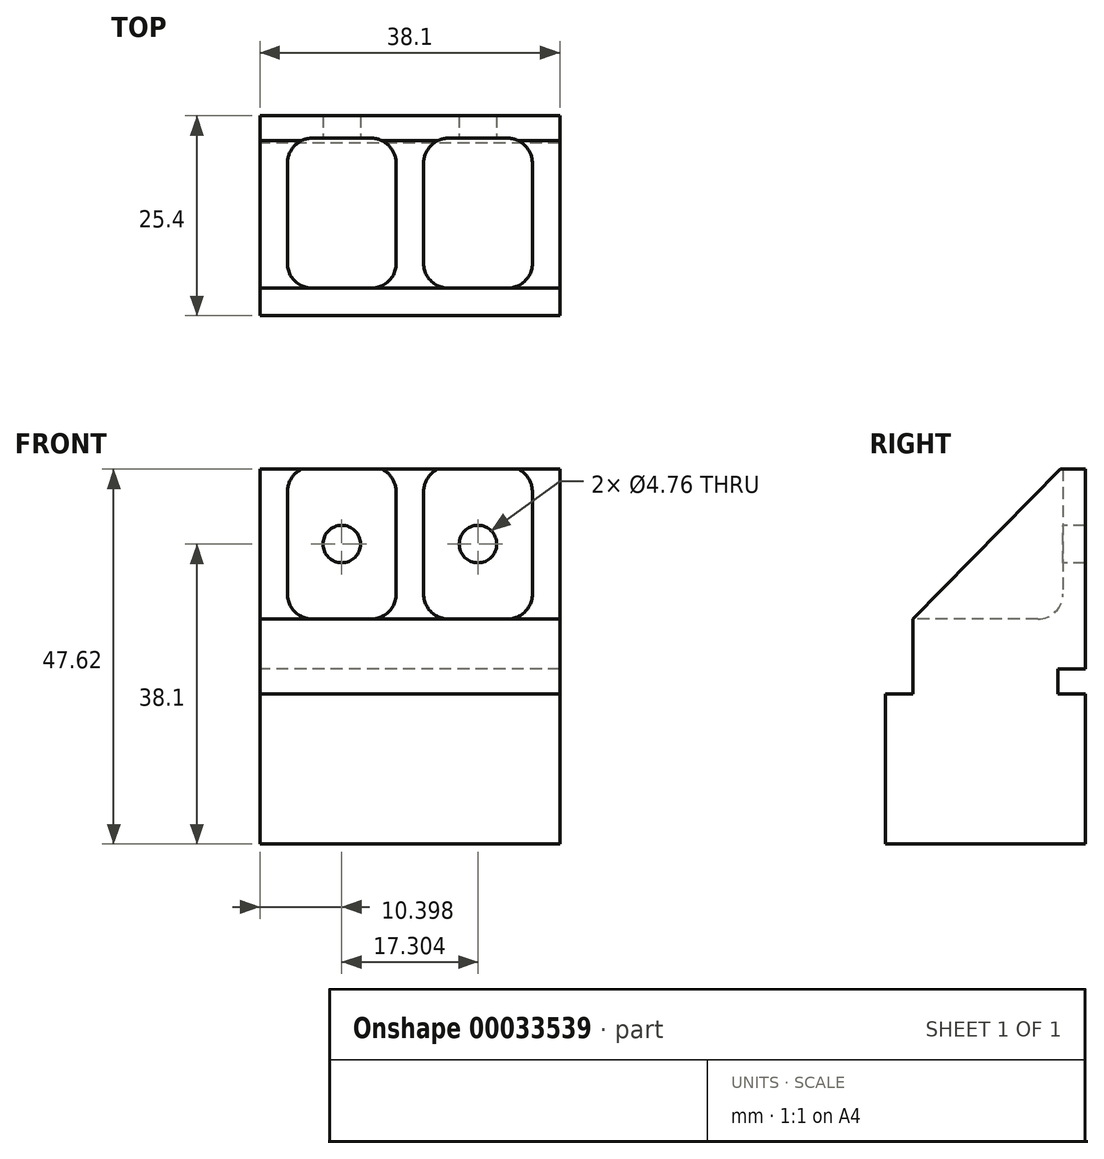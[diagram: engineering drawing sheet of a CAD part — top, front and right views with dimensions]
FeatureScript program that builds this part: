
annotation { "Feature Type Name" : "Feature", "Feature Type Description" : "" }
export const myFeature = defineFeature(function(context is Context, id is Id, definition is map)
    precondition{}
    {
        {
            var Q0;
            Q0=qCreatedBy(makeId("Right.planeOp"),FACE);
            var sketch = newSketch(context, id + "F0", { "sketchPlane" : qUnion([Q0])});
            skLineSegment(sketch, "E0.bottom", {"start": v(0, 0) * mm, "end": v(25.4, 0) * mm});
            skLineSegment(sketch, "E0.top", {"start": v(0, 19.05) * mm, "end": v(3.5, 19.05) * mm});
            skLineSegment(sketch, "E0.left", {"start": v(0, 0) * mm, "end": v(0, 19.05) * mm});
            skLineSegment(sketch, "E0.right", {"start": v(25.4, 0) * mm, "end": v(25.4, 19.05) * mm});
            skLineSegment(sketch, "E1", {"start": v(21.9, 19.05) * mm, "end": v(21.9, 22.23) * mm});
            skLineSegment(sketch, "E2", {"start": v(21.9, 22.23) * mm, "end": v(25.4, 22.23) * mm});
            skLineSegment(sketch, "E3", {"start": v(25.4, 22.23) * mm, "end": v(25.4, 47.62) * mm});
            skLineSegment(sketch, "E4", {"start": v(25.4, 47.62) * mm, "end": v(22.23, 47.62) * mm});
            skLineSegment(sketch, "E5", {"start": v(22.23, 47.62) * mm, "end": v(22.23, 28.58) * mm});
            skLineSegment(sketch, "E6", {"start": v(22.23, 28.58) * mm, "end": v(3.5, 28.57) * mm});
            skLineSegment(sketch, "E7", {"start": v(3.5, 28.57) * mm, "end": v(3.5, 19.05) * mm});
            skLineSegment(sketch, "E8.trimOffspring", {"start": v(21.9, 19.05) * mm, "end": v(25.4, 19.05) * mm});
            skLineSegment(sketch, "E9", {"start": v(3.5, 28.57) * mm, "end": v(22.23, 47.62) * mm});
            skSolve(sketch);
        }
        {
            var Q0;
            Q0=makeQuery(id+"F0.imprint","IMPRINT",FACE,{"disambiguationData":[TD([[makeQuery(id+"F0.imprint","IMPRINT",EDGE,{"derivedFrom":sQuery(id+"F0.wireOp",EDGE,"E0.bottom")}),1.0]])]});
            var Q1;
            Q1=makeQuery(id+"F0.imprint","IMPRINT",FACE,{"disambiguationData":[TD([[makeQuery(id+"F0.imprint","IMPRINT",EDGE,{"derivedFrom":sQuery(id+"F0.wireOp",EDGE,"E5")}),-1.0]])]});
            extrude(context, id + "F1", {"entities" : qUnion([Q0, Q1]), "depth" : 38.1 * mm});
        }
        {
            var Q0;
            Q0=makeQuery(id+"F1.opExtrude","SWEPT_FACE",FACE,{"disambiguationData":[OSD([sQuery(id+"F0.wireOp",EDGE,"E7")])]});
            var sketch = newSketch(context, id + "F2", { "sketchPlane" : qUnion([Q0])});
            skLineSegment(sketch, "E10.bottom", {"start": v(3.5, 47.62) * mm, "end": v(17.3, 47.62) * mm});
            skLineSegment(sketch, "E10.top", {"start": v(3.5, 28.57) * mm, "end": v(17.3, 28.57) * mm});
            skLineSegment(sketch, "E10.left", {"start": v(3.5, 47.62) * mm, "end": v(3.5, 28.57) * mm});
            skLineSegment(sketch, "E10.right", {"start": v(17.3, 47.62) * mm, "end": v(17.3, 28.57) * mm});
            skLineSegment(sketch, "E11.bottom", {"start": v(20.8, 47.62) * mm, "end": v(34.6, 47.62) * mm});
            skLineSegment(sketch, "E11.top", {"start": v(20.8, 28.57) * mm, "end": v(34.6, 28.57) * mm});
            skLineSegment(sketch, "E11.left", {"start": v(20.8, 47.62) * mm, "end": v(20.8, 28.57) * mm});
            skLineSegment(sketch, "E11.right", {"start": v(34.6, 47.62) * mm, "end": v(34.6, 28.57) * mm});
            skSolve(sketch);
        }
        {
            var Q0;
            Q0=makeQuery(id+"F2.imprint","IMPRINT",FACE,{"disambiguationData":[TD([[makeQuery(id+"F2.imprint","IMPRINT",EDGE,{"derivedFrom":sQuery(id+"F2.wireOp",EDGE,"E11.bottom")}),-1.0]])]});
            var Q1;
            Q1=makeQuery(id+"F2.imprint","IMPRINT",FACE,{"disambiguationData":[TD([[makeQuery(id+"F2.imprint","IMPRINT",EDGE,{"derivedFrom":sQuery(id+"F2.wireOp",EDGE,"E10.bottom")}),-1.0]])]});
            extrude(context, id + "F3", {"entities" : qUnion([Q0, Q1]), "operationType" : NewBodyOperationType.REMOVE, "oppositeDirection" : true, "depth" : 19.05 * mm});
        }
        {
            var Q0;
            Q0=makeQuery(id+"F3.boolean.opBoolean","COPY",EDGE,{"derivedFrom":makeQuery(id+"F3.opExtrude","CAP_EDGE",EDGE,{"disambiguationData":[OSD([sQuery(id+"F2.wireOp",EDGE,"E10.top")])],"isStart":false})});
            var Q1;
            Q1=makeQuery(id+"F3.boolean.opBoolean","COPY",EDGE,{"derivedFrom":makeQuery(id+"F3.opExtrude","CAP_EDGE",EDGE,{"disambiguationData":[OSD([sQuery(id+"F2.wireOp",EDGE,"E11.top")])],"isStart":false})});
            var Q2;
            Q2=makeQuery(id+"F3.boolean.opBoolean","COPY",EDGE,{"derivedFrom":makeQuery(id+"F3.opExtrude","CAP_EDGE",EDGE,{"disambiguationData":[OSD([sQuery(id+"F2.wireOp",EDGE,"E11.left")])],"isStart":false})});
            var Q3;
            Q3=makeQuery(id+"F3.boolean.opBoolean","COPY",EDGE,{"derivedFrom":makeQuery(id+"F3.opExtrude","SWEPT_EDGE",EDGE,{"disambiguationData":[OSD([sQuery(id+"F0.wireOp",EDGE,"E6"),sQuery(id+"F0.wireOp",EDGE,"E7"),sQuery(id+"F0.wireOp",EDGE,"E9"),sQuery(id+"F2.wireOp",EDGE,"E11.top"),sQuery(id+"F2.wireOp",EDGE,"E11.left")])]})});
            var Q4;
            Q4=makeQuery(id+"F3.boolean.opBoolean","COPY",EDGE,{"derivedFrom":makeQuery(id+"F3.opExtrude","CAP_EDGE",EDGE,{"disambiguationData":[OSD([sQuery(id+"F2.wireOp",EDGE,"E10.left")])],"isStart":false})});
            var Q5;
            Q5=makeQuery(id+"F3.boolean.opBoolean","COPY",EDGE,{"derivedFrom":makeQuery(id+"F3.opExtrude","SWEPT_EDGE",EDGE,{"disambiguationData":[OSD([sQuery(id+"F0.wireOp",EDGE,"E6"),sQuery(id+"F0.wireOp",EDGE,"E7"),sQuery(id+"F0.wireOp",EDGE,"E9"),sQuery(id+"F2.wireOp",EDGE,"E10.top"),sQuery(id+"F2.wireOp",EDGE,"E10.left")])]})});
            var Q6;
            Q6=makeQuery(id+"F3.boolean.opBoolean","COPY",EDGE,{"derivedFrom":makeQuery(id+"F3.opExtrude","SWEPT_EDGE",EDGE,{"disambiguationData":[OSD([sQuery(id+"F0.wireOp",EDGE,"E6"),sQuery(id+"F0.wireOp",EDGE,"E7"),sQuery(id+"F0.wireOp",EDGE,"E9"),sQuery(id+"F2.wireOp",EDGE,"E11.top"),sQuery(id+"F2.wireOp",EDGE,"E11.right")])]})});
            var Q7;
            Q7=makeQuery(id+"F3.boolean.opBoolean","COPY",EDGE,{"derivedFrom":makeQuery(id+"F3.opExtrude","CAP_EDGE",EDGE,{"disambiguationData":[OSD([sQuery(id+"F2.wireOp",EDGE,"E11.right")])],"isStart":false})});
            var Q8;
            Q8=makeQuery(id+"F3.boolean.opBoolean","COPY",EDGE,{"derivedFrom":makeQuery(id+"F3.opExtrude","SWEPT_EDGE",EDGE,{"disambiguationData":[OSD([sQuery(id+"F0.wireOp",EDGE,"E6"),sQuery(id+"F0.wireOp",EDGE,"E7"),sQuery(id+"F0.wireOp",EDGE,"E9"),sQuery(id+"F2.wireOp",EDGE,"E10.top"),sQuery(id+"F2.wireOp",EDGE,"E10.right")])]})});
            var Q9;
            Q9=makeQuery(id+"F3.boolean.opBoolean","COPY",EDGE,{"derivedFrom":makeQuery(id+"F3.opExtrude","CAP_EDGE",EDGE,{"disambiguationData":[OSD([sQuery(id+"F2.wireOp",EDGE,"E10.right")])],"isStart":false})});
            fillet(context, id + "F4", {"entities" : qUnion([Q0, Q1, Q2, Q3, Q4, Q5, Q6, Q7, Q8, Q9]), "radius" : 3.17 * mm, "tangentPropagation" : true, "allowEdgeOverflow" : false});
        }
        {
            var Q0;
            Q0=makeQuery(id+"F3.boolean.opBoolean","COPY",FACE,{"derivedFrom":makeQuery(id+"F3.opExtrude","CAP_FACE",FACE,{"disambiguationData":[OSD([sQuery(id+"F2.wireOp",EDGE,"E10.bottom"),sQuery(id+"F2.wireOp",EDGE,"E10.top"),sQuery(id+"F2.wireOp",EDGE,"E10.left"),sQuery(id+"F2.wireOp",EDGE,"E10.right")])],"isStart":false})});
            var sketch = newSketch(context, id + "F5", { "sketchPlane" : qUnion([Q0])});
            skCircle(sketch, "E12", {"center": v(10.4, 38.1) * mm, "radius": 2.38 * mm});
            skCircle(sketch, "E13", {"center": v(27.7, 38.1) * mm, "radius": 2.38 * mm});
            skLineSegment(sketch, "E14", {"start": v(10.4, 38.1) * mm, "end": v(10.4, 31.75) * mm});
            skPoint(sketch, "E14.endSnap0", {"position": v(10.4, 31.75) * mm});
            skLineSegment(sketch, "E15", {"start": v(27.7, 38.1) * mm, "end": v(27.7, 31.75) * mm});
            skSolve(sketch);
        }
        {
            var Q0;
            Q0 = qSketchRegion(id + "F5", true);
            extrude(context, id + "F6", {"entities" : qUnion([Q0]), "operationType" : NewBodyOperationType.REMOVE, "endBound" : BoundingType.THROUGH_ALL, "oppositeDirection" : true, "depth" : 25.4 * mm});
        }
    });
